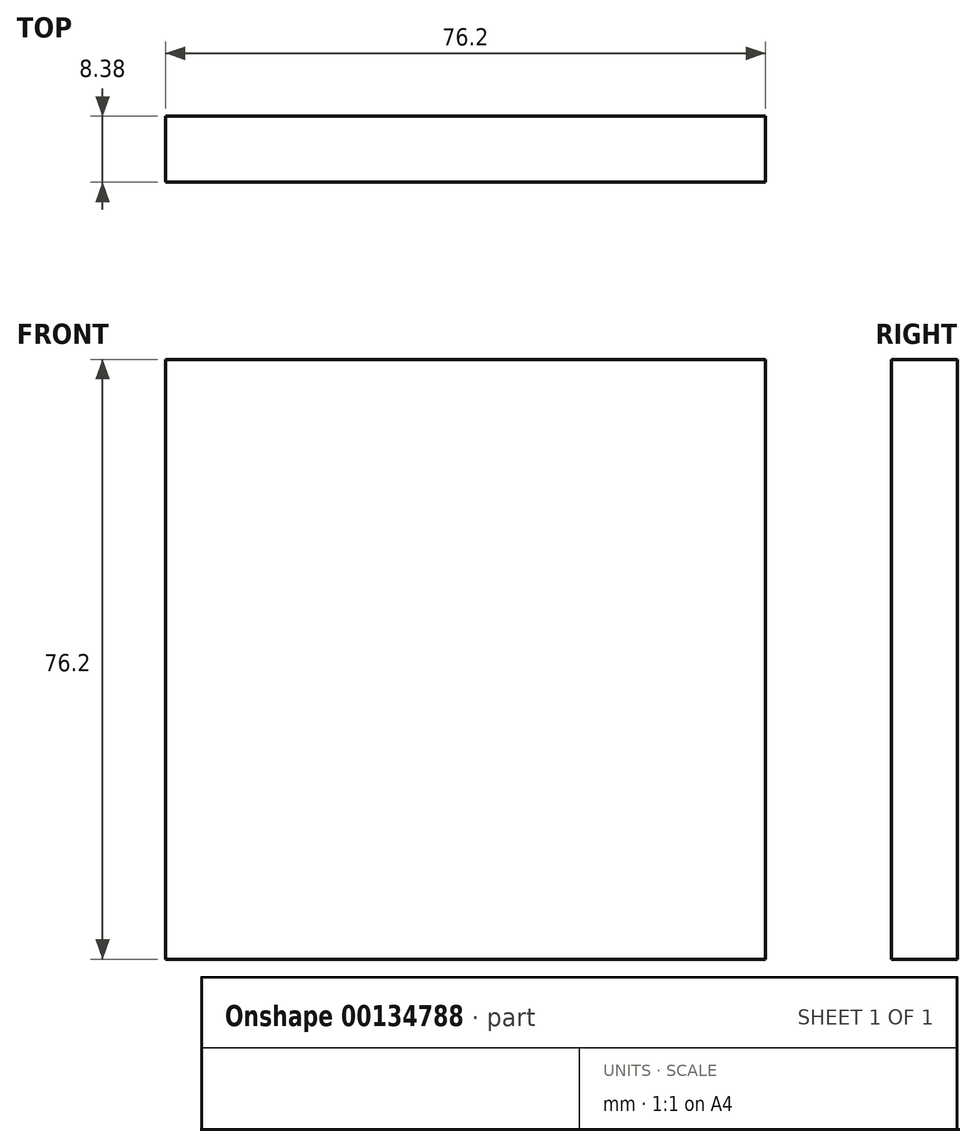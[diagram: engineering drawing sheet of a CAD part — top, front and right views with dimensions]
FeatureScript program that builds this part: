
annotation { "Feature Type Name" : "Feature", "Feature Type Description" : "" }
export const myFeature = defineFeature(function(context is Context, id is Id, definition is map)
    precondition{}
    {
        {
            var Q0;
            Q0=qCreatedBy(makeId("Front.planeOp"),FACE);
            var sketch = newSketch(context, id + "F0", { "sketchPlane" : qUnion([Q0])});
            skLineSegment(sketch, "E0.bottom", {"start": v(-38.31, 38.1) * mm, "end": v(37.89, 38.1) * mm});
            skLineSegment(sketch, "E0.top", {"start": v(-38.31, -38.1) * mm, "end": v(37.89, -38.1) * mm});
            skLineSegment(sketch, "E0.left", {"start": v(-38.31, 38.1) * mm, "end": v(-38.31, -38.1) * mm});
            skLineSegment(sketch, "E0.right", {"start": v(37.89, 38.1) * mm, "end": v(37.89, -38.1) * mm});
            skSolve(sketch);
        }
        {
            var Q0;
            Q0=makeQuery(id+"F0.imprint","IMPRINT",FACE,{"disambiguationData":[TD([[makeQuery(id+"F0.imprint","IMPRINT",EDGE,{"derivedFrom":sQuery(id+"F0.wireOp",EDGE,"E0.bottom")}),-1.0]])]});
            extrude(context, id + "F1", {"entities" : qUnion([Q0]), "depth" : 8.38 * mm});
        }
    });
